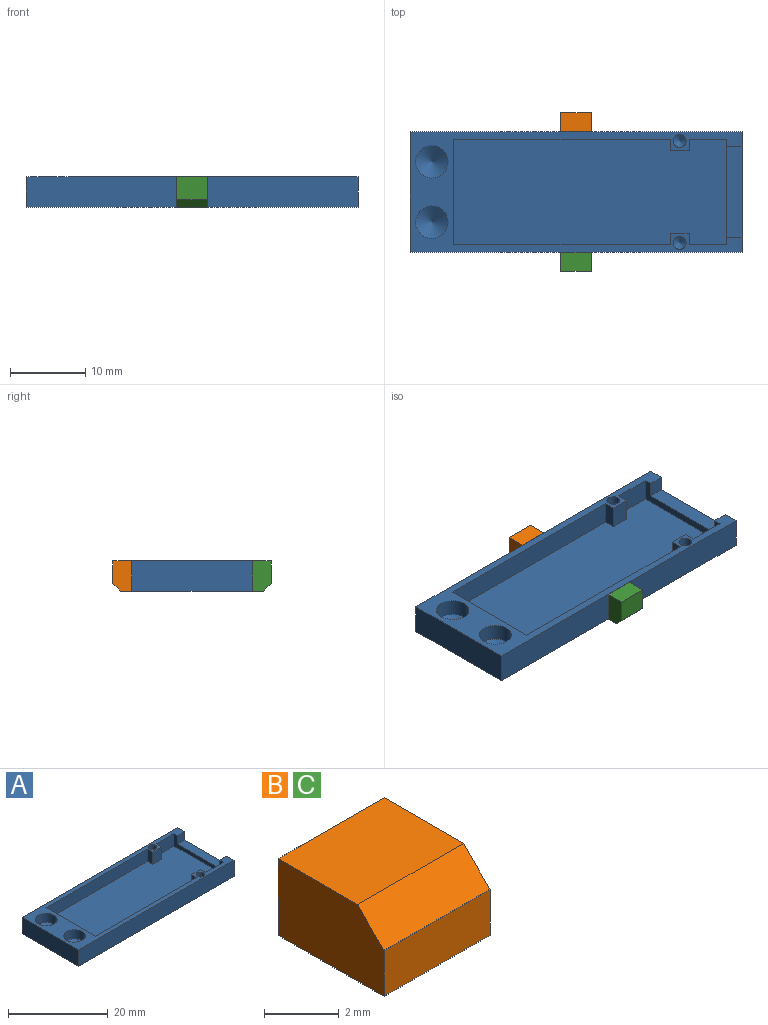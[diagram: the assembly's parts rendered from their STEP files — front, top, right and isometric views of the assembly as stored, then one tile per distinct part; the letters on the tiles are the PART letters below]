
ASSEMBLY  parts=3 mates=4
PART A: 30 faces, bbox 44x16x4 mm
  f0: plane 36.21x14mm, normal (0,0,1), area 499.4mm2, adj f1,f2,f4,f5,f6,f15,f16,f17
  f1: plane 28.71x3mm, normal (0,1,0), area 86.1mm2, adj f0,f12,f20,f21
  f2: plane 28.71x3mm, normal (0,-1,0), area 86.1mm2, adj f0,f12,f15,f21
  f3: plane 2x2mm, normal (0,1,0), area 4mm2, adj f6,f8,f12,f14
  f4: plane 5x3mm, normal (0,1,0), area 15mm2, adj f0,f6,f12,f18
  f5: plane 5x3mm, normal (0,-1,0), area 15mm2, adj f0,f6,f12,f16
  f6: plane 14x3mm, normal (-1,0,0), area 18mm2, adj f0,f3,f4,f5,f7,f12,f14
  f7: plane 2x2mm, normal (0,-1,0), area 4mm2, adj f6,f8,f12,f14
  f8: plane 16x4mm, normal (1,0,0), area 40mm2, adj f3,f7,f9,f11,f12,f13,f14
  f9: plane 44x4mm, normal (0,1,0), area 176mm2, adj f8,f10,f12,f13
  f10: plane 16x4mm, normal (-1,0,0), area 64mm2, adj f9,f11,f12,f13
  f11: plane 44x4mm, normal (0,-1,0), area 176mm2, adj f8,f10,f12,f13
  f12: plane 44x16mm, normal (0,0,1), area 147mm2, adj f1,f2,f3,f4,f5,f6,f7,f8
  f13: plane 44x16mm, normal (0,0,-1), area 704mm2, adj f8,f9,f10,f11
  f14: plane 12x2mm, normal (0,0,1), area 24mm2, adj f3,f6,f7,f8
  f15: plane 3x1.5mm, normal (-1,0,0), area 4.5mm2, adj f0,f2,f12,f17
  f16: plane 3x1.5mm, normal (1,0,0), area 4.5mm2, adj f0,f5,f12,f17
  f17: plane 3x2.5mm, normal (0,-1,0), area 7.5mm2, adj f0,f12,f15,f16
  f18: plane 3x1.5mm, normal (1,0,0), area 4.5mm2, adj f0,f4,f12,f19
  f19: plane 3x2.5mm, normal (0,1,0), area 7.5mm2, adj f0,f12,f18,f20
  f20: plane 3x1.5mm, normal (-1,0,0), area 4.5mm2, adj f0,f1,f12,f19
  f21: plane 14x3mm, normal (1,0,0), area 42mm2, adj f0,f1,f2,f12
  f22: cone r=0mm half-angle=59deg, axis (0,0,1), area 16.9mm2, adj f23
  f23: cylinder r=2.15mm len=4.3mm, axis (0,0,1), area 29.7mm2, adj f12,f22
  f24: cone r=0mm half-angle=59deg, axis (0,0,1), area 16.9mm2, adj f25
  f25: cylinder r=2.15mm len=4.3mm, axis (0,0,1), area 29.7mm2, adj f12,f24
  f26: cone r=0mm half-angle=59deg, axis (0,0,1), area 2.6mm2, adj f27
  f27: cylinder r=0.85mm len=2.2mm, axis (0,0,1), area 11.7mm2, adj f12,f26
  f28: cone r=0mm half-angle=59deg, axis (0,0,1), area 2.6mm2, adj f29
  f29: cylinder r=0.85mm len=2.2mm, axis (0,0,1), area 11.7mm2, adj f12,f28
PART B: 7 faces, bbox 4x4x2.5 mm
  f0: plane 4x2.5mm, normal (-1,0,0), area 9.5mm2, adj f1,f3,f4,f5,f6
  f1: plane 4x1.5mm, normal (0,-1,0), area 6mm2, adj f0,f2,f5,f6
  f2: plane 4x2.5mm, normal (1,0,0), area 9.5mm2, adj f1,f3,f4,f5,f6
  f3: plane 4x2.5mm, normal (0,1,0), area 10mm2, adj f0,f2,f4,f5
  f4: plane 4x3mm, normal (0,0,1), area 12mm2, adj f0,f2,f3,f6
  f5: plane 4x4mm, normal (0,0,-1), area 16mm2, adj f0,f1,f2,f3
  f6: plane 4x1mm, normal (0,-0.71,0.71), area 5.7mm2, adj f0,f1,f2,f4
PART C: same geometry as B
PLACE A t=(14.61,9.43,-7.33)mm
PLACE B rot(axis=(0,-0.71,-0.71),180deg) t=(36.61,24.43,-7.33)mm
PLACE C rot(axis=(1,0,0),90deg) t=(32.61,8.43,-7.33)mm
MATE parallel C.f5 <-> A.f11  axis (0,1,0) through (34.61,8.43,-5.33)mm
MATE planar B.f5 <-> A.f9  axis (0,-1,0) through (34.61,24.43,-5.33)mm
MATE planar C.f5 <-> A.f11  axis (0,1,0) through (34.61,8.43,-5.33)mm
MATE parallel B.f5 <-> A.f9  axis (0,-1,0) through (34.61,24.43,-5.33)mm
